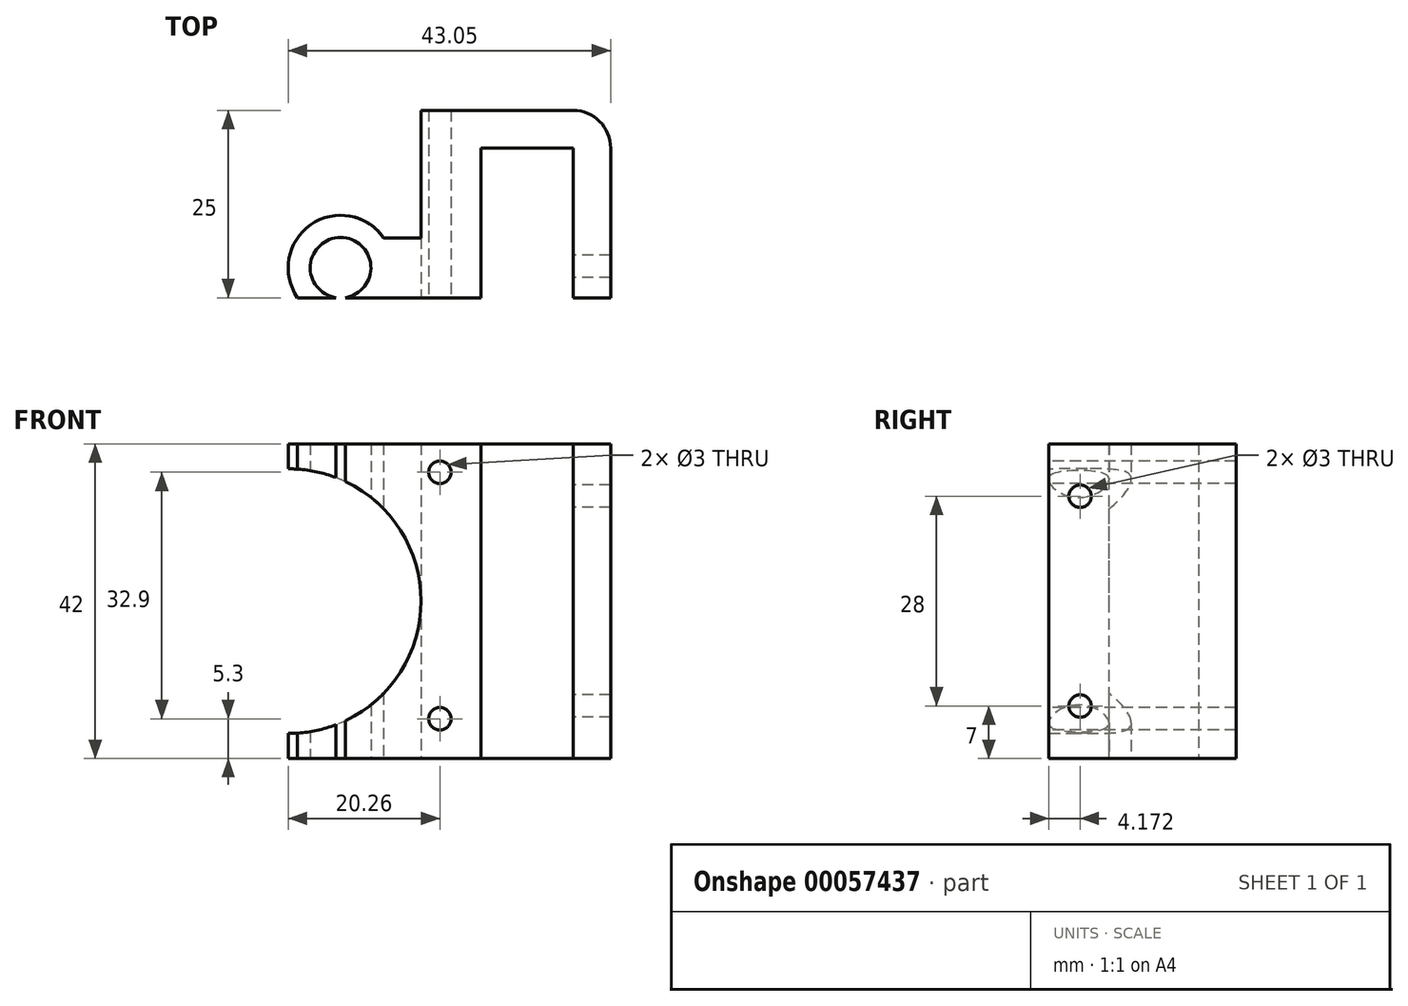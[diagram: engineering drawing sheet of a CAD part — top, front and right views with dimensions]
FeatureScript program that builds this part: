
annotation { "Feature Type Name" : "Feature", "Feature Type Description" : "" }
export const myFeature = defineFeature(function(context is Context, id is Id, definition is map)
    precondition{}
    {
        {
            var Q0;
            Q0=qCreatedBy(makeId("Top.planeOp"),FACE);
            var sketch = newSketch(context, id + "F0", { "sketchPlane" : qUnion([Q0])});
            skLineSegment(sketch, "E0.bottom", {"start": v(-7.51, 0) * mm, "end": v(22.79, 0) * mm});
            skLineSegment(sketch, "E0.top", {"start": v(-2.51, 25) * mm, "end": v(17.79, 25) * mm});
            skLineSegment(sketch, "E0.left", {"start": v(-7.51, 0) * mm, "end": v(-7.51, 8) * mm});
            skLineSegment(sketch, "E0.right", {"start": v(22.79, 0) * mm, "end": v(22.79, 20) * mm});
            skLineSegment(sketch, "E1", {"start": v(17.79, 0) * mm, "end": v(17.79, 20) * mm});
            skLineSegment(sketch, "E2", {"start": v(17.79, 20) * mm, "end": v(5.49, 20) * mm});
            skLineSegment(sketch, "E3", {"start": v(5.49, 20) * mm, "end": v(5.49, 0) * mm});
            skLineSegment(sketch, "E4", {"start": v(5.49, 0) * mm, "end": v(17.79, 0) * mm});
            skLineSegment(sketch, "E5", {"start": v(-2.51, 25) * mm, "end": v(-2.51, 0) * mm});
            skLineSegment(sketch, "E6", {"start": v(-7.51, 8) * mm, "end": v(-2.51, 8) * mm});
            skCircle(sketch, "E7", {"center": v(-13.26, 4) * mm, "radius": 4.05 * mm});
            skCircle(sketch, "E8", {"center": v(-13.26, 4) * mm, "radius": 7 * mm});
            skLineSegment(sketch, "E9", {"start": v(-7.51, 0) * mm, "end": v(-19, 0) * mm});
            skPoint(sketch, "E10.visualSharp", {"position": v(22.79, 25) * mm});
            skArc(sketch, "E10.filletArc", {"start": v(22.79, 20) * mm, "mid": v(21.32, 23.54) * mm, "end": v(17.79, 25) * mm});
            skSolve(sketch);
        }
        {
            var Q0;
            {var subQ2=sQuery(id+"F0.wireOp",EDGE,"E0.left");Q0=makeQuery(id+"F0.imprint","IMPRINT",FACE,{"disambiguationData":[TD([[makeQuery(id+"F0.imprint","IMPRINT",EDGE,{"derivedFrom":subQ2}),1.0]])]});}
            var Q1;
            {var subQ6=sQuery(id+"F0.wireOp",EDGE,"E6");Q1=makeQuery(id+"F0.imprint","IMPRINT",FACE,{"disambiguationData":[TD([[makeQuery(id+"F0.imprint","IMPRINT",EDGE,{"derivedFrom":subQ6}),-1.0]])]});}
            var Q2;
            {var subQ0=sQuery(id+"F0.wireOp",EDGE,"E0.left");Q2=makeQuery(id+"F0.imprint","IMPRINT",FACE,{"disambiguationData":[TD([[makeQuery(id+"F0.imprint","IMPRINT",EDGE,{"derivedFrom":subQ0}),-1.0]])]});}
            var Q3;
            {var subQ1=sQuery(id+"F0.wireOp",EDGE,"E0.top");Q3=makeQuery(id+"F0.imprint","IMPRINT",FACE,{"disambiguationData":[TD([[makeQuery(id+"F0.imprint","IMPRINT",EDGE,{"derivedFrom":subQ1}),-1.0]])]});}
            extrude(context, id + "F1", {"entities" : qUnion([Q0, Q1, Q2, Q3]), "depth" : 42 * mm});
        }
        {
            var Q0;
            Q0=qCreatedBy(makeId("Front.planeOp"),FACE);
            var sketch = newSketch(context, id + "F2", { "sketchPlane" : qUnion([Q0])});
            skCircle(sketch, "E11", {"center": v(-20.17, 21) * mm, "radius": 17.65 * mm});
            skLineSegment(sketch, "E12", {"start": v(-20.17, 42) * mm, "end": v(-20.17, 0) * mm});
            skCircle(sketch, "E13", {"center": v(0, 38.2) * mm, "radius": 1.5 * mm});
            skCircle(sketch, "E14", {"center": v(0, 5.3) * mm, "radius": 1.5 * mm});
            skLineSegment(sketch, "E15", {"start": v(-20.17, 21) * mm, "end": v(0, 21) * mm});
            skSolve(sketch);
        }
        {
            var Q0;
            {var subQ0=sQuery(id+"F2.wireOp",EDGE,"E12");var subQ1=sQuery(id+"F2.wireOp",EDGE,"E11");var subQ2=makeQuery(id+"F2.imprint","INTERSECT",VERTEX,{"disambiguationData":[OD(0.0)],"derivedFrom":[subQ1,subQ0]});Q0=makeQuery(id+"F2.imprint","IMPRINT",FACE,{"disambiguationData":[TD([[makeQuery(id+"F2.imprint","IMPRINT",EDGE,{"disambiguationData":[TD([[subQ2,-1.0]])],"derivedFrom":subQ1}),1.0]])]});}
            var Q1;
            {var subQ0=sQuery(id+"F2.wireOp",EDGE,"E15");var subQ1=sQuery(id+"F2.wireOp",EDGE,"E11");var subQ2=makeQuery(id+"F2.imprint","INTERSECT",VERTEX,{"derivedFrom":[subQ1,subQ0]});Q1=makeQuery(id+"F2.imprint","IMPRINT",FACE,{"disambiguationData":[TD([[makeQuery(id+"F2.imprint","IMPRINT",EDGE,{"disambiguationData":[TD([[subQ2,1.0]])],"derivedFrom":subQ1}),1.0]])]});}
            var Q2;
            Q2=makeQuery(id+"F2.imprint","IMPRINT",FACE,{"disambiguationData":[TD([[makeQuery(id+"F2.imprint","IMPRINT",EDGE,{"derivedFrom":sQuery(id+"F2.wireOp",EDGE,"E13")}),1.0]])]});
            var Q3;
            Q3=makeQuery(id+"F2.imprint","IMPRINT",FACE,{"disambiguationData":[TD([[makeQuery(id+"F2.imprint","IMPRINT",EDGE,{"derivedFrom":sQuery(id+"F2.wireOp",EDGE,"E14")}),1.0]])]});
            var Q4;
            {var subQ0=sQuery(id+"F2.wireOp",EDGE,"E12");var subQ1=sQuery(id+"F2.wireOp",EDGE,"E11");var subQ2=makeQuery(id+"F2.imprint","INTERSECT",VERTEX,{"disambiguationData":[OD(0.0)],"derivedFrom":[subQ1,subQ0]});Q4=makeQuery(id+"F2.imprint","IMPRINT",FACE,{"disambiguationData":[TD([[makeQuery(id+"F2.imprint","IMPRINT",EDGE,{"disambiguationData":[TD([[subQ2,1.0]])],"derivedFrom":subQ1}),1.0]])]});}
            extrude(context, id + "F3", {"entities" : qUnion([Q0, Q1, Q2, Q3, Q4]), "operationType" : NewBodyOperationType.REMOVE, "endBound" : BoundingType.THROUGH_ALL, "oppositeDirection" : true, "depth" : 25 * mm, "hasSecondDirection" : true, "secondDirectionBound" : BoundingType.THROUGH_ALL, "secondDirectionOppositeDirection" : false, "secondDirectionDepth" : 25 * mm});
        }
        {
            var Q0;
            Q0=qCreatedBy(makeId("Right.planeOp"),FACE);
            cPlane(context, id + "F4", {"entities" : qUnion([Q0]), "cplaneType" : CPlaneType.OFFSET, "offset" : 10 * mm, "width" : 150 * mm, "height" : 150 * mm});
        }
        {
            var Q0;
            Q0=qCreatedBy(id+"F4.planeOp",FACE);
            var sketch = newSketch(context, id + "F5", { "sketchPlane" : qUnion([Q0])});
            skCircle(sketch, "E16", {"center": v(4.17, 7) * mm, "radius": 1.5 * mm});
            skLineSegment(sketch, "E17", {"start": v(4.17, 0) * mm, "end": v(4.17, 7) * mm});
            skLineSegment(sketch, "E18", {"start": v(4.17, 42) * mm, "end": v(4.17, 35) * mm});
            skCircle(sketch, "E19", {"center": v(4.17, 35) * mm, "radius": 1.5 * mm});
            skSolve(sketch);
        }
        {
            var Q0;
            Q0=makeQuery(id+"F5.imprint","IMPRINT",FACE,{"disambiguationData":[TD([[makeQuery(id+"F5.imprint","IMPRINT",EDGE,{"derivedFrom":sQuery(id+"F5.wireOp",EDGE,"E16")}),1.0]])]});
            var Q1;
            Q1=makeQuery(id+"F5.imprint","IMPRINT",FACE,{"disambiguationData":[TD([[makeQuery(id+"F5.imprint","IMPRINT",EDGE,{"derivedFrom":sQuery(id+"F5.wireOp",EDGE,"E19")}),1.0]])]});
            extrude(context, id + "F6", {"entities" : qUnion([Q0, Q1]), "operationType" : NewBodyOperationType.REMOVE, "depth" : 25 * mm});
        }
    });
